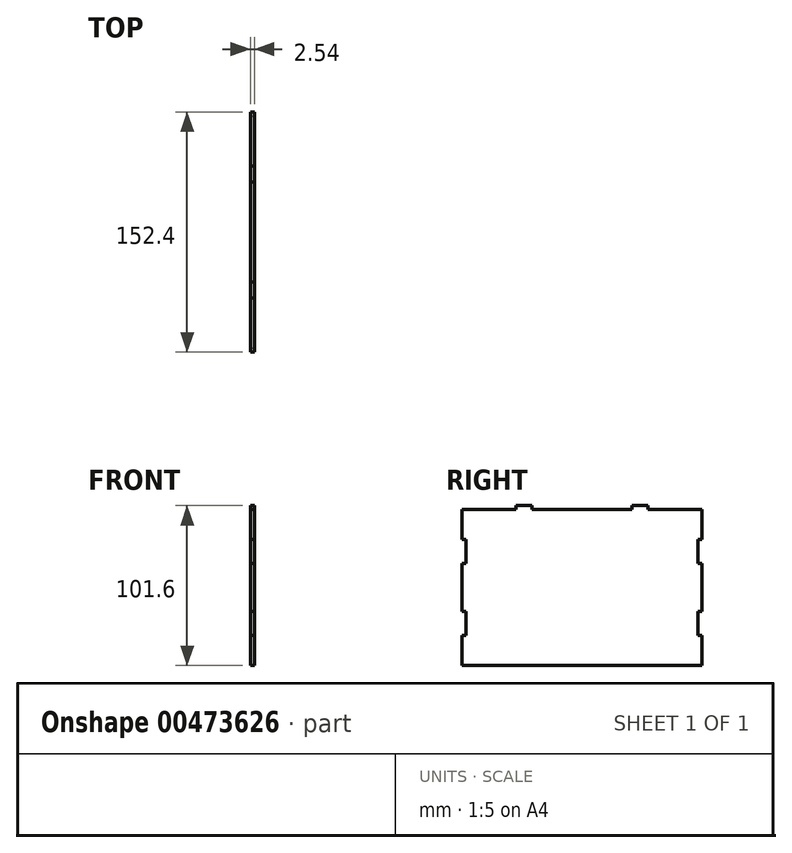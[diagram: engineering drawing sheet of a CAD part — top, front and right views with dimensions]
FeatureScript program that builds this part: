
annotation { "Feature Type Name" : "Feature", "Feature Type Description" : "" }
export const myFeature = defineFeature(function(context is Context, id is Id, definition is map)
    precondition{}
    {
        {
            var Q0;
            Q0=qCreatedBy(makeId("Right.planeOp"),FACE);
            var sketch = newSketch(context, id + "F0", { "sketchPlane" : qUnion([Q0])});
            skLineSegment(sketch, "E0.bottom", {"start": v(76.2, -50.8) * mm, "end": v(-76.2, -50.8) * mm});
            skLineSegment(sketch, "E0.top", {"start": v(76.2, 50.8) * mm, "end": v(-76.2, 50.8) * mm});
            skLineSegment(sketch, "E0.left", {"start": v(76.2, -50.8) * mm, "end": v(76.2, 50.8) * mm});
            skLineSegment(sketch, "E0.right", {"start": v(-76.2, -50.8) * mm, "end": v(-76.2, 50.8) * mm});
            skPoint(sketch, "E0.middle", {"position": v(0, 0) * mm});
            skSolve(sketch);
        }
        {
            var Q0;
            Q0=makeQuery(id+"F0.imprint","IMPRINT",FACE,{"disambiguationData":[TD([[makeQuery(id+"F0.imprint","IMPRINT",EDGE,{"derivedFrom":sQuery(id+"F0.wireOp",EDGE,"E0.bottom")}),-1.0]])]});
            extrude(context, id + "F1", {"entities" : qUnion([Q0]), "depth" : 2.54 * mm});
        }
        {
            var Q0;
            Q0=makeQuery(id+"F1.opExtrude","CAP_FACE",FACE,{"disambiguationData":[OSD([sQuery(id+"F0.wireOp",EDGE,"E0.bottom"),sQuery(id+"F0.wireOp",EDGE,"E0.top"),sQuery(id+"F0.wireOp",EDGE,"E0.left"),sQuery(id+"F0.wireOp",EDGE,"E0.right")])],"isStart":false});
            var sketch = newSketch(context, id + "F2", { "sketchPlane" : qUnion([Q0])});
            skLineSegment(sketch, "E1", {"start": v(-76.2, 50.8) * mm, "end": v(-76.2, 48.26) * mm});
            skLineSegment(sketch, "E2", {"start": v(-76.2, 48.26) * mm, "end": v(-41.9, 48.26) * mm});
            skLineSegment(sketch, "E3", {"start": v(-41.9, 48.26) * mm, "end": v(-41.9, 50.8) * mm});
            skLineSegment(sketch, "E4", {"start": v(-41.9, 50.8) * mm, "end": v(-76.2, 50.8) * mm});
            skLineSegment(sketch, "E5", {"start": v(-31.75, 50.8) * mm, "end": v(-31.75, 48.26) * mm});
            skLineSegment(sketch, "E6", {"start": v(-31.75, 48.26) * mm, "end": v(31.75, 48.26) * mm});
            skLineSegment(sketch, "E7", {"start": v(31.75, 48.26) * mm, "end": v(31.75, 50.8) * mm});
            skLineSegment(sketch, "E8", {"start": v(31.75, 50.8) * mm, "end": v(-31.75, 50.8) * mm});
            skLineSegment(sketch, "E9", {"start": v(76.2, 50.8) * mm, "end": v(41.9, 50.8) * mm});
            skLineSegment(sketch, "E10", {"start": v(41.9, 50.8) * mm, "end": v(41.9, 48.26) * mm});
            skLineSegment(sketch, "E11", {"start": v(41.9, 48.26) * mm, "end": v(76.2, 48.26) * mm});
            skLineSegment(sketch, "E12", {"start": v(76.2, 48.26) * mm, "end": v(76.2, 50.8) * mm});
            skSolve(sketch);
        }
        {
            var Q0;
            Q0 = qSketchRegion(id + "F2", true);
            extrude(context, id + "F3", {"entities" : qUnion([Q0]), "operationType" : NewBodyOperationType.REMOVE, "oppositeDirection" : true, "depth" : 25.4 * mm});
        }
        {
            var Q0;
            Q0=makeQuery(id+"F1.opExtrude","CAP_FACE",FACE,{"disambiguationData":[OSD([sQuery(id+"F0.wireOp",EDGE,"E0.bottom"),sQuery(id+"F0.wireOp",EDGE,"E0.top"),sQuery(id+"F0.wireOp",EDGE,"E0.left"),sQuery(id+"F0.wireOp",EDGE,"E0.right")])],"isStart":false});
            var sketch = newSketch(context, id + "F4", { "sketchPlane" : qUnion([Q0])});
            skLineSegment(sketch, "E13", {"start": v(76.2, 29.2) * mm, "end": v(73.66, 29.2) * mm});
            skLineSegment(sketch, "E14", {"start": v(73.66, 29.21) * mm, "end": v(73.66, 13.97) * mm});
            skLineSegment(sketch, "E15", {"start": v(73.66, 13.97) * mm, "end": v(76.2, 13.97) * mm});
            skLineSegment(sketch, "E16", {"start": v(76.2, 13.97) * mm, "end": v(76.2, 29.2) * mm});
            skLineSegment(sketch, "E17", {"start": v(76.2, -16.51) * mm, "end": v(73.66, -16.51) * mm});
            skLineSegment(sketch, "E18", {"start": v(73.66, -16.5) * mm, "end": v(73.66, -31.75) * mm});
            skLineSegment(sketch, "E19", {"start": v(73.66, -31.75) * mm, "end": v(76.2, -31.75) * mm});
            skLineSegment(sketch, "E20", {"start": v(76.2, -31.75) * mm, "end": v(76.2, -16.51) * mm});
            skSolve(sketch);
        }
        {
            var Q0;
            Q0 = qSketchRegion(id + "F4", true);
            extrude(context, id + "F5", {"entities" : qUnion([Q0]), "operationType" : NewBodyOperationType.REMOVE, "oppositeDirection" : true, "depth" : 25.4 * mm});
        }
        {
            var Q0;
            Q0=makeQuery(id+"F1.opExtrude","CAP_FACE",FACE,{"disambiguationData":[OSD([sQuery(id+"F0.wireOp",EDGE,"E0.bottom"),sQuery(id+"F0.wireOp",EDGE,"E0.top"),sQuery(id+"F0.wireOp",EDGE,"E0.left"),sQuery(id+"F0.wireOp",EDGE,"E0.right")])],"isStart":false});
            var sketch = newSketch(context, id + "F6", { "sketchPlane" : qUnion([Q0])});
            skLineSegment(sketch, "E21", {"start": v(-76.2, 29.2) * mm, "end": v(-73.66, 29.2) * mm});
            skLineSegment(sketch, "E22", {"start": v(-73.66, 29.2) * mm, "end": v(-73.66, 13.97) * mm});
            skLineSegment(sketch, "E23", {"start": v(-73.66, 13.97) * mm, "end": v(-76.2, 13.97) * mm});
            skLineSegment(sketch, "E24", {"start": v(-76.2, 13.97) * mm, "end": v(-76.2, 29.2) * mm});
            skLineSegment(sketch, "E25", {"start": v(-76.2, -16.51) * mm, "end": v(-73.66, -16.51) * mm});
            skLineSegment(sketch, "E26", {"start": v(-73.66, -16.51) * mm, "end": v(-73.66, -31.75) * mm});
            skLineSegment(sketch, "E27", {"start": v(-73.66, -31.75) * mm, "end": v(-76.2, -31.75) * mm});
            skLineSegment(sketch, "E28", {"start": v(-76.2, -31.75) * mm, "end": v(-76.2, -16.51) * mm});
            skSolve(sketch);
        }
        {
            var Q0;
            Q0 = qSketchRegion(id + "F6", true);
            extrude(context, id + "F7", {"entities" : qUnion([Q0]), "operationType" : NewBodyOperationType.REMOVE, "oppositeDirection" : true, "depth" : 25.4 * mm});
        }
    });
